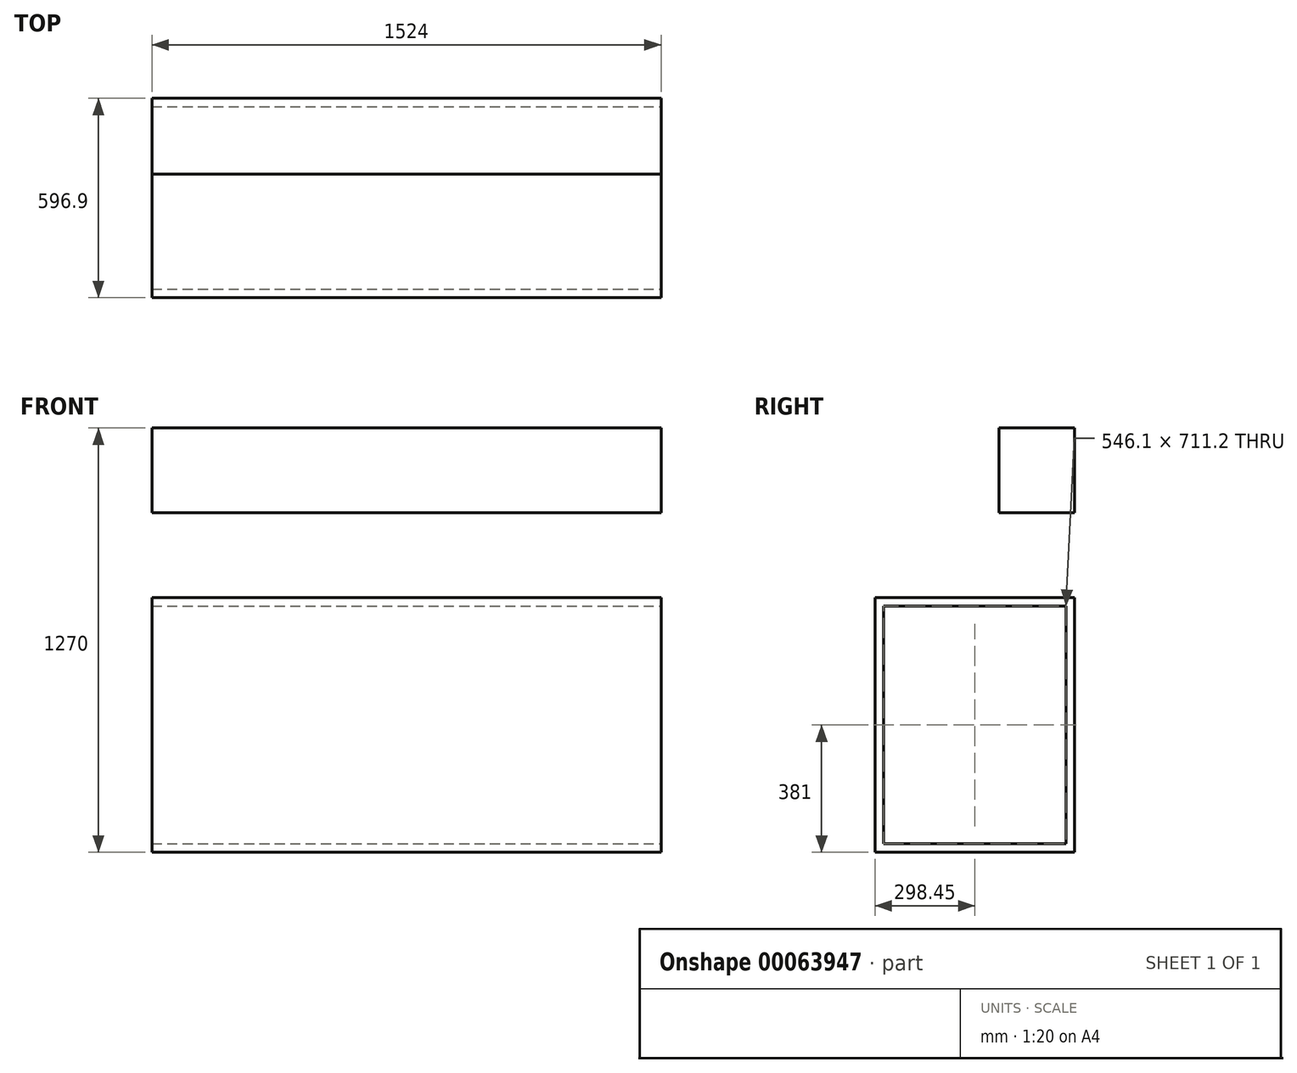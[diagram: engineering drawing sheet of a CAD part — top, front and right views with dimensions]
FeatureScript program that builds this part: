
annotation { "Feature Type Name" : "Feature", "Feature Type Description" : "" }
export const myFeature = defineFeature(function(context is Context, id is Id, definition is map)
    precondition{}
    {
        {
            var Q0;
            Q0=qCreatedBy(makeId("Right.planeOp"),FACE);
            var sketch = newSketch(context, id + "F0", { "sketchPlane" : qUnion([Q0])});
            skLineSegment(sketch, "E0", {"start": v(0, 0) * mm, "end": v(-596.9, 0) * mm});
            skLineSegment(sketch, "E1", {"start": v(-596.9, 0) * mm, "end": v(-596.9, -762) * mm});
            skLineSegment(sketch, "E2", {"start": v(-596.9, -762) * mm, "end": v(0, -762) * mm});
            skLineSegment(sketch, "E3", {"start": v(0, -762) * mm, "end": v(0, 0) * mm});
            skLineSegment(sketch, "E4", {"start": v(0, 0) * mm, "end": v(0, 508) * mm});
            skPoint(sketch, "E5", {"position": v(0, 254) * mm});
            skPoint(sketch, "E6", {"position": v(0, 381) * mm});
            skPoint(sketch, "E7", {"position": v(0, 127) * mm});
            skLineSegment(sketch, "E8", {"start": v(0, 254) * mm, "end": v(-226.44, 254) * mm});
            skLineSegment(sketch, "E9", {"start": v(-226.44, 254) * mm, "end": v(-226.44, 508) * mm});
            skLineSegment(sketch, "E10", {"start": v(-226.44, 508) * mm, "end": v(0, 508) * mm});
            skSolve(sketch);
        }
        {
            var Q0;
            Q0=makeQuery(id+"F0.imprint","IMPRINT",FACE,{"disambiguationData":[TD([[makeQuery(id+"F0.imprint","IMPRINT",EDGE,{"derivedFrom":sQuery(id+"F0.wireOp",EDGE,"E0")}),1.0]])]});
            var Q1;
            {var subQ2=sQuery(id+"F0.wireOp",EDGE,"E8");Q1=makeQuery(id+"F0.imprint","IMPRINT",FACE,{"disambiguationData":[TD([[makeQuery(id+"F0.imprint","IMPRINT",EDGE,{"derivedFrom":subQ2}),-1.0]])]});}
            extrude(context, id + "F1", {"entities" : qUnion([Q0, Q1]), "depth" : 1524 * mm});
        }
        {
            var Q0;
            Q0=makeQuery(id+"F1.opExtrude","CAP_FACE",FACE,{"disambiguationData":[OSD([sQuery(id+"F0.wireOp",EDGE,"E4"),sQuery(id+"F0.wireOp",EDGE,"E8"),sQuery(id+"F0.wireOp",EDGE,"E9"),sQuery(id+"F0.wireOp",EDGE,"E10")])],"isStart":false});
            var sketch = newSketch(context, id + "F2", { "sketchPlane" : qUnion([Q0])});
            skPoint(sketch, "E11", {"position": v(0, 0) * mm});
            skPoint(sketch, "E12", {"position": v(-25.4, 0) * mm});
            skPoint(sketch, "E13", {"position": v(0, -25.4) * mm});
            skLineSegment(sketch, "E14", {"start": v(0, -25.4) * mm, "end": v(-617.95, -25.4) * mm, "construction": true});
            skLineSegment(sketch, "E15", {"start": v(-25.4, 0) * mm, "end": v(-25.4, -783.88) * mm, "construction": true});
            skLineSegment(sketch, "E16.bottom", {"start": v(-25.4, -25.4) * mm, "end": v(-571.5, -25.4) * mm});
            skLineSegment(sketch, "E16.top", {"start": v(-25.4, -736.6) * mm, "end": v(-571.5, -736.6) * mm});
            skLineSegment(sketch, "E16.left", {"start": v(-25.4, -25.4) * mm, "end": v(-25.4, -736.6) * mm});
            skLineSegment(sketch, "E16.right", {"start": v(-571.5, -25.4) * mm, "end": v(-571.5, -736.6) * mm});
            skSolve(sketch);
        }
        {
            var Q0;
            Q0=makeQuery(id+"F2.imprint","IMPRINT",FACE,{"disambiguationData":[TD([[makeQuery(id+"F2.imprint","IMPRINT",EDGE,{"derivedFrom":sQuery(id+"F2.wireOp",EDGE,"E16.bottom")}),1.0]])]});
            extrude(context, id + "F3", {"entities" : qUnion([Q0]), "operationType" : NewBodyOperationType.REMOVE, "oppositeDirection" : true, "depth" : 1693.75 * mm});
        }
    });
